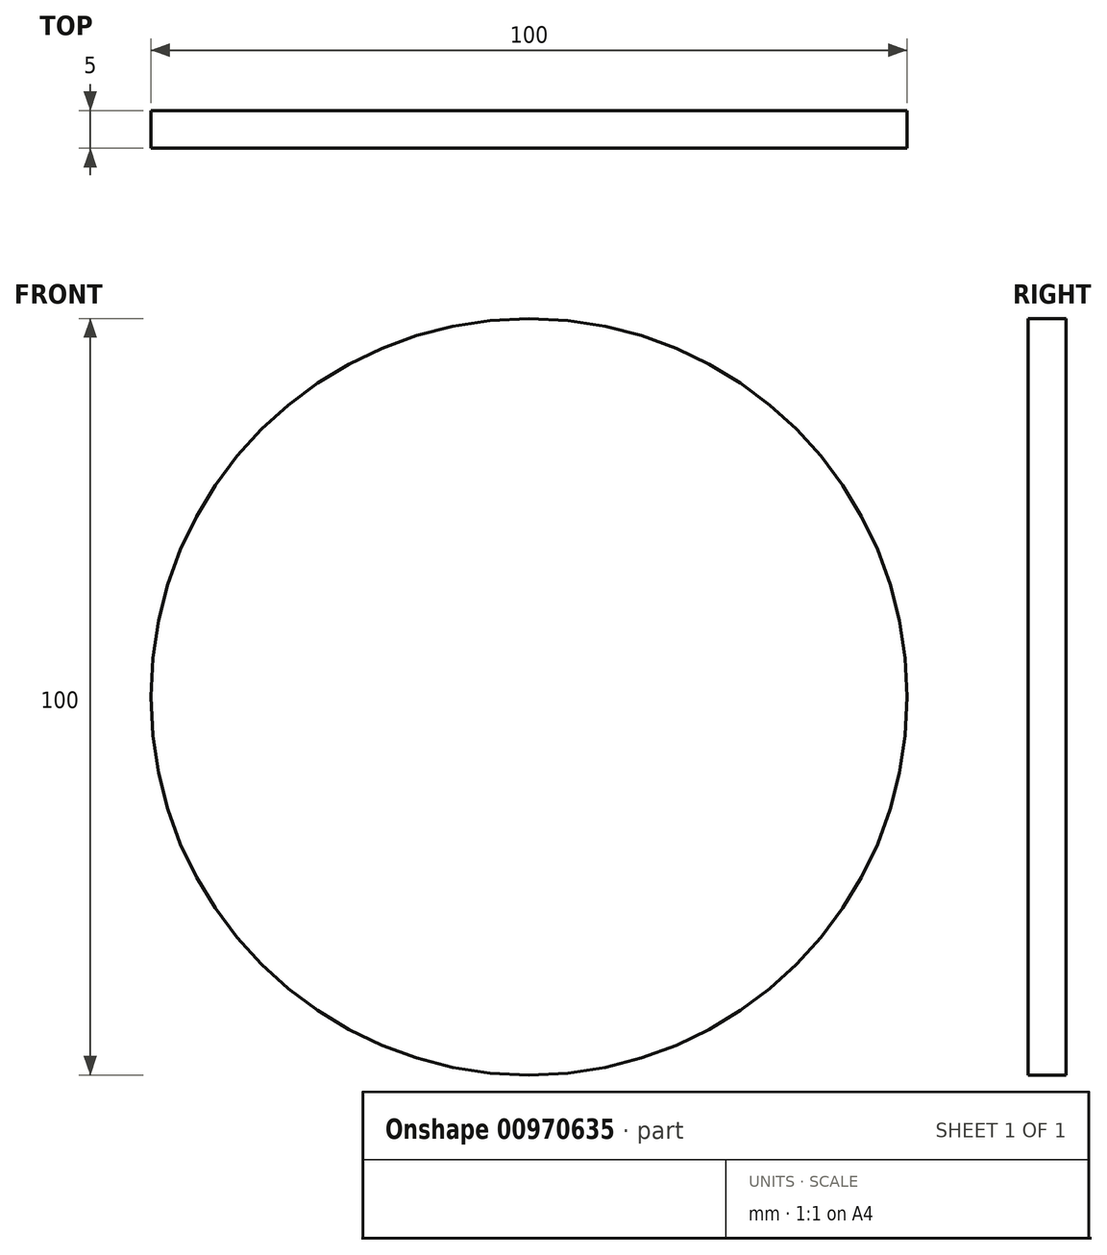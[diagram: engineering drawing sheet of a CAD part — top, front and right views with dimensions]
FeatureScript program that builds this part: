
annotation { "Feature Type Name" : "Feature", "Feature Type Description" : "" }
export const myFeature = defineFeature(function(context is Context, id is Id, definition is map)
    precondition{}
    {
        {
            var Q0;
            Q0=qCreatedBy(makeId("Front.planeOp"),FACE);
            var sketch = newSketch(context, id + "F0", { "sketchPlane" : qUnion([Q0])});
            skCircle(sketch, "E0", {"center": v(0, 0) * mm, "radius": 50 * mm});
            skSolve(sketch);
        }
        {
            var Q0;
            Q0 = qSketchRegion(id + "F0", true);
            extrude(context, id + "F1", {"entities" : qUnion([Q0]), "depth" : 5 * mm, "offsetDistance" : 25.4 * mm});
        }
    });
